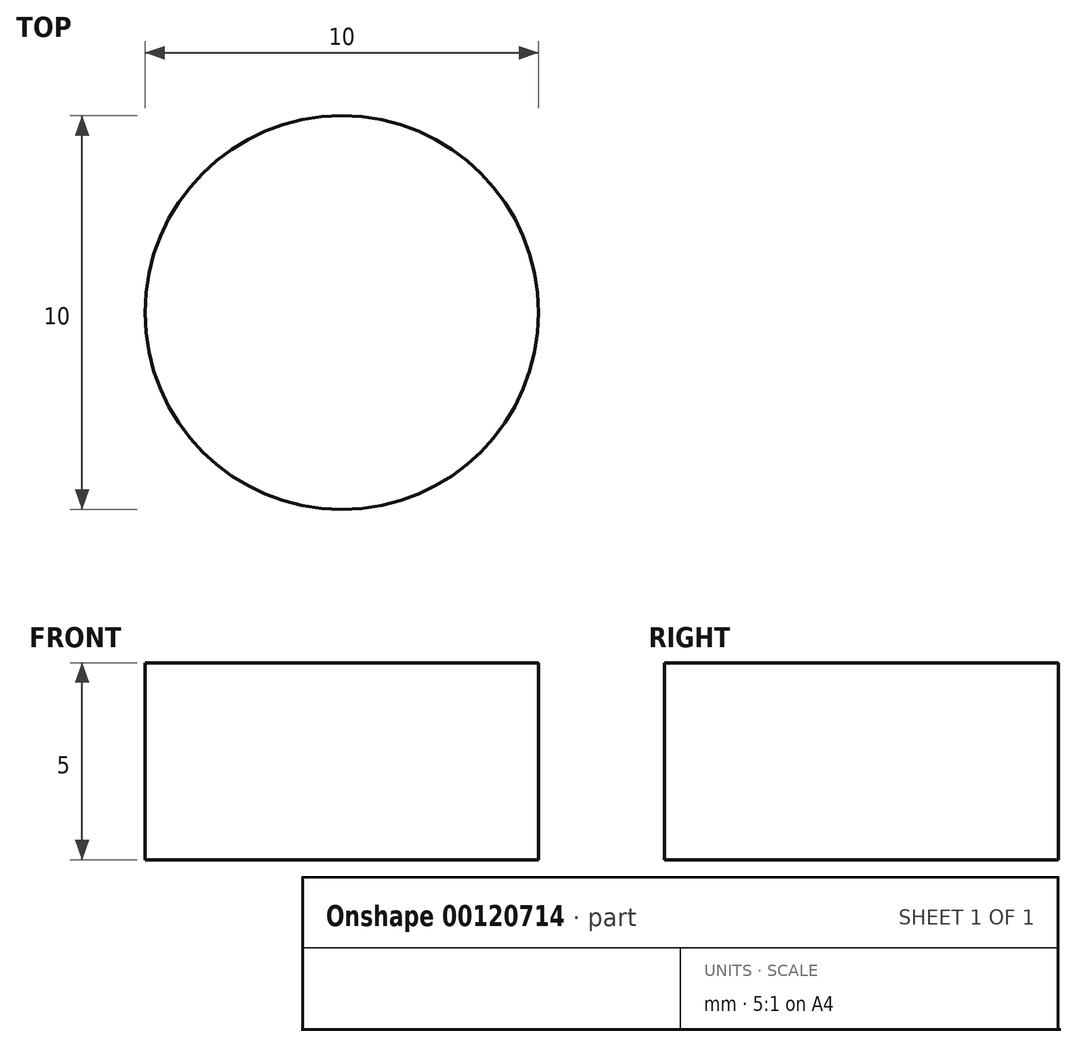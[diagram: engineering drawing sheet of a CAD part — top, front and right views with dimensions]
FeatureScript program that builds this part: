
annotation { "Feature Type Name" : "Feature", "Feature Type Description" : "" }
export const myFeature = defineFeature(function(context is Context, id is Id, definition is map)
    precondition{}
    {
        {
            var Q0;
            Q0=qCreatedBy(makeId("Top.planeOp"),FACE);
            var sketch = newSketch(context, id + "F0", { "sketchPlane" : qUnion([Q0])});
            skCircle(sketch, "E0", {"center": v(0, 0) * mm, "radius": 5 * mm});
            skSolve(sketch);
        }
        {
            var Q0;
            Q0 = qSketchRegion(id + "F0", true);
            extrude(context, id + "F1", {"entities" : qUnion([Q0]), "depth" : 2.5 * mm, "hasSecondDirection" : true, "secondDirectionOppositeDirection" : true, "secondDirectionDepth" : 2.5 * mm});
        }
    });
